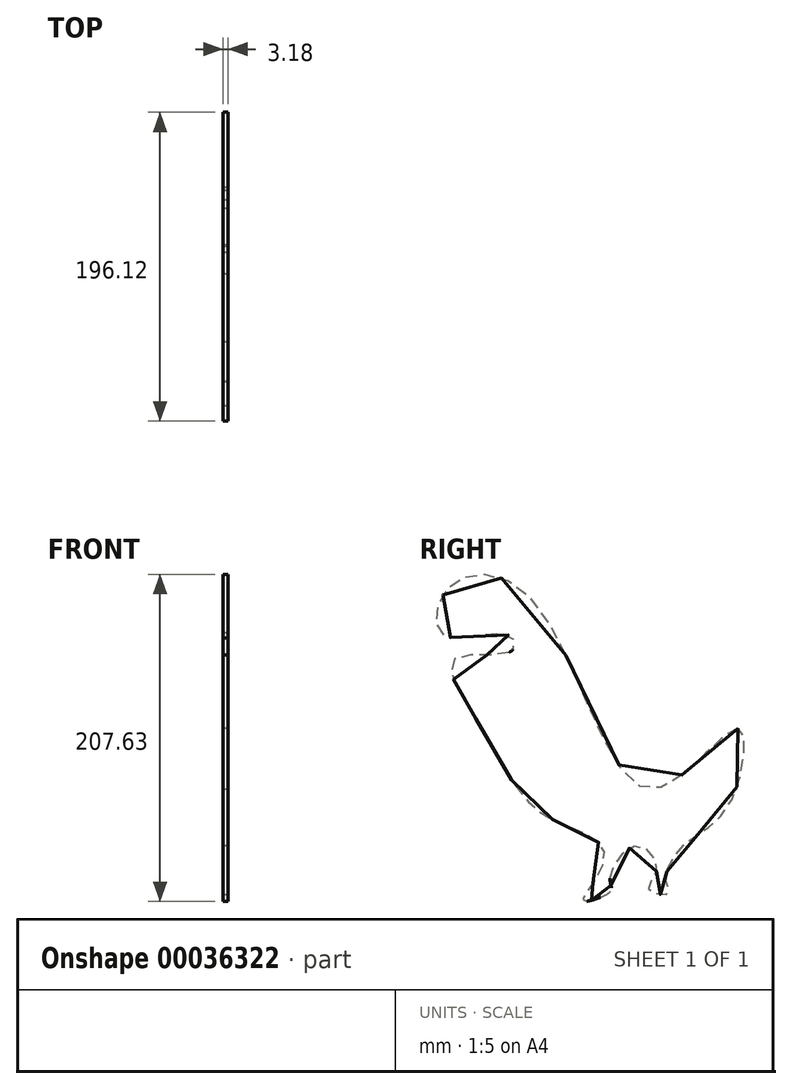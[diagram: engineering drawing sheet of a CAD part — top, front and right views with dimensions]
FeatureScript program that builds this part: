
annotation { "Feature Type Name" : "Feature", "Feature Type Description" : "" }
export const myFeature = defineFeature(function(context is Context, id is Id, definition is map)
    precondition{}
    {
        {
            var Q0;
            Q0=qCreatedBy(makeId("Right.planeOp"),FACE);
            var sketch = newSketch(context, id + "F0", { "sketchPlane" : qUnion([Q0])});
            skLineSegment(sketch, "E0.rect.bottom", {"start": v(-127, 127) * mm, "end": v(127, 127) * mm});
            skLineSegment(sketch, "E0.rect.top", {"start": v(-127, -127) * mm, "end": v(127, -127) * mm});
            skLineSegment(sketch, "E0.rect.left", {"start": v(-127, 127) * mm, "end": v(-127, -127) * mm});
            skLineSegment(sketch, "E0.rect.right", {"start": v(127, 127) * mm, "end": v(127, -127) * mm});
            skPoint(sketch, "E0.rect.middle", {"position": v(0, 0) * mm});
            skSolve(sketch);
        }
        {
            var Q0;
            Q0=makeQuery(id+"F0.imprint","IMPRINT",FACE,{"disambiguationData":[TD([[makeQuery(id+"F0.imprint","IMPRINT",EDGE,{"derivedFrom":sQuery(id+"F0.wireOp",EDGE,"E0.rect.bottom")}),-1.0]])]});
            var sketch = newSketch(context, id + "F1", { "sketchPlane" : qUnion([Q0])});
            skFitSpline(sketch, "E1", {"points": [v(122.54, 3.24) * mm, v(67.3, -35.46) * mm, v(-8.98, 86) * mm, v(-62.02, 91.72) * mm, v(-64.24, 62.23) * mm, v(-23.53, 62.9) * mm, v(-21.66, 52.07) * mm, v(-59.38, 45.05) * mm, v(-44.41, 11.06) * mm, v(-44.41, 10.68) * mm, v(-15.62, -37.15) * mm, v(10.91, -57.36) * mm, v(37.07, -73.47) * mm, v(29.24, -96.96) * mm, v(24.39, -106.29) * mm, v(35.22, -104.07) * mm, v(42.31, -99.23) * mm, v(41.56, -91.76) * mm, v(57.98, -71.27) * mm, v(71.06, -86.6) * mm, v(65.84, -98.9) * mm, v(78.17, -101.92) * mm, v(77.04, -93.7) * mm, v(88.23, -70.96) * mm, v(117.72, -44.15) * mm, v(122.54, 3.24) * mm]});
            skSolve(sketch);
        }
        {
            var Q0;
            Q0=makeQuery(id+"F1.imprint","IMPRINT",FACE,{"disambiguationData":[TD([[makeQuery(id+"F1.imprint","IMPRINT",EDGE,{"derivedFrom":sQuery(id+"F1.wireOp",EDGE,"E1")}),1.0]])]});
            var sketch = newSketch(context, id + "F2", { "sketchPlane" : qUnion([Q0])});
            skSolve(sketch);
        }
        {
            var Q0;
            Q0=makeQuery(id+"F1.imprint","IMPRINT",FACE,{"disambiguationData":[TD([[makeQuery(id+"F1.imprint","IMPRINT",EDGE,{"derivedFrom":sQuery(id+"F1.wireOp",EDGE,"E1")}),1.0]])]});
            extrude(context, id + "F3", {"entities" : qUnion([Q0]), "depth" : 3.17 * mm});
        }
    });
